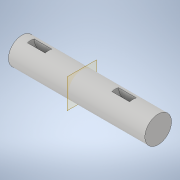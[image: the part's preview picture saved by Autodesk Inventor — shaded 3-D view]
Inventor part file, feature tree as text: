
AUTODESK INVENTOR PART (.ipt)
format: ipt  version: 2021 (Build 250183000, 183)  size: 118,272 bytes
history: native  units: in
note: dims shown in document units (in); Inventor stores cm internally (conversion verified against a paired STEP export)
features: extrude x3, sketch x3, plane x1, mirror x1
ambient origin geometry x8: Origin, YZ Plane, XZ Plane, XY Plane, X Axis, Y Axis, Z Axis, Center Point
bodies: Solid1 (feature_tree)
feature tree (8):
  extrude  "Extrusion1"  Depth=3.375in TaperAngle=0.0deg
  extrude  "Extrusion3"  Depth=0.5in
  plane  "Work Plane1"
  mirror  "Mirror1"
  extrude  "Extrusion4"  [1 undecoded]
  sketch  "Sketch1"  dims[d0=0.75in d1=3.375in d2=0.0in]
  sketch  "Sketch3"  dims[d7=0.5in d8=0.5in]
  sketch  "Sketch4"  dims[d9=0.188in d10=0.0in d11=-1.6878in d12=0.459in d13=0.0in]
note: 1 required parameter value undecoded (feature->parameter linkage not recoverable at this tier; creation-order binding heuristic only, values carry confidence <= 0.55)
